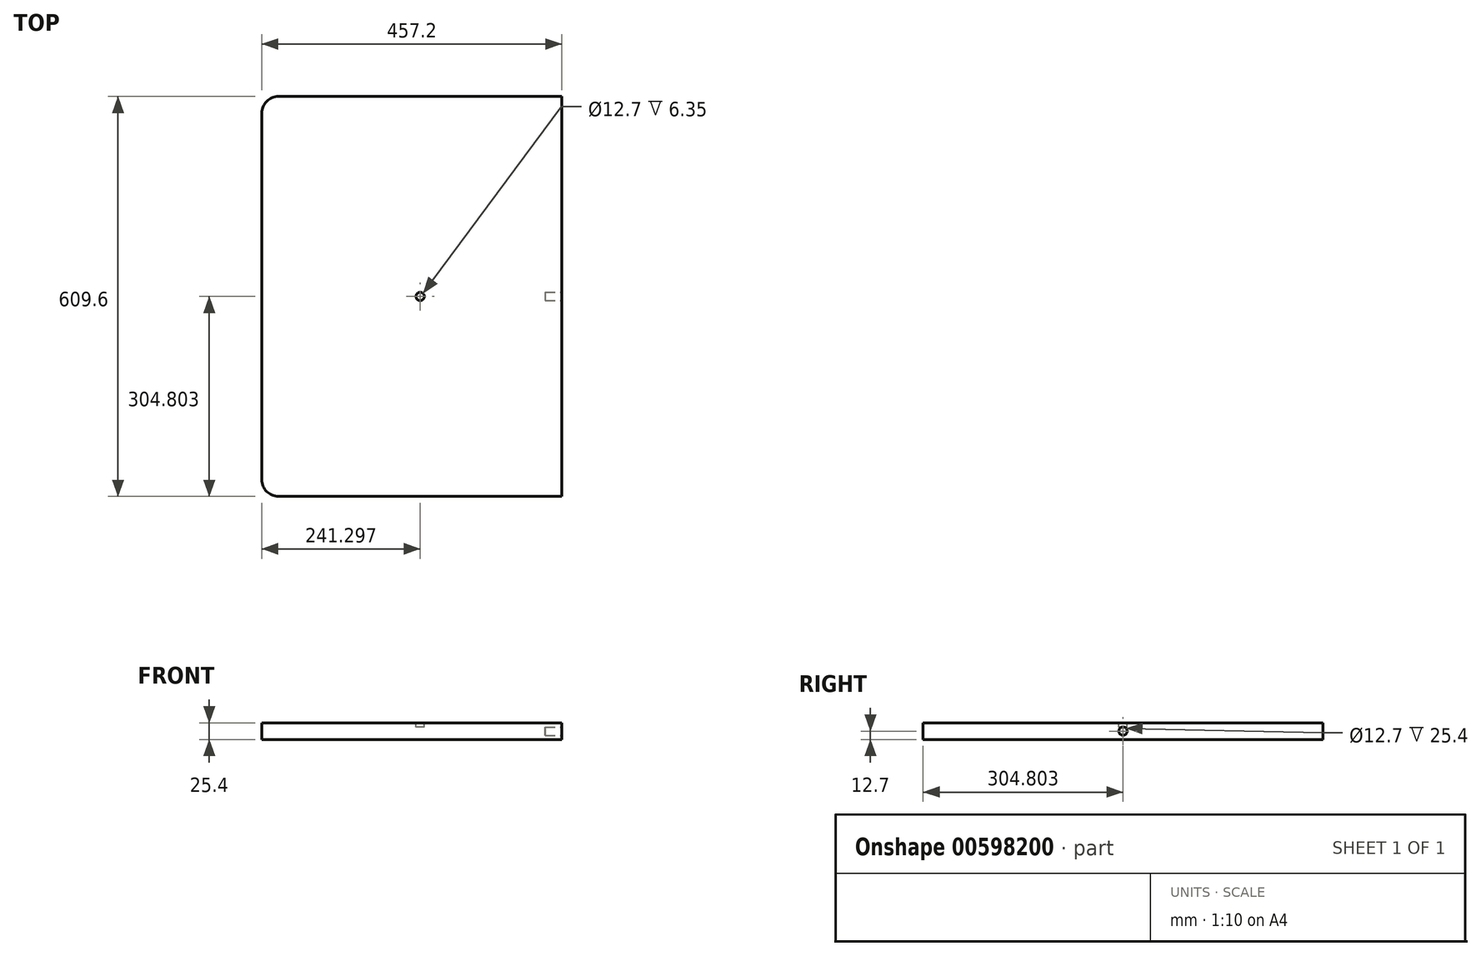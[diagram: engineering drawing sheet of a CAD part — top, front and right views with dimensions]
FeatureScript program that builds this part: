
annotation { "Feature Type Name" : "Feature", "Feature Type Description" : "" }
export const myFeature = defineFeature(function(context is Context, id is Id, definition is map)
    precondition{}
    {
        {
            var Q0;
            Q0=qCreatedBy(makeId("Top.planeOp"),FACE);
            var sketch = newSketch(context, id + "F0", { "sketchPlane" : qUnion([Q0])});
            skLineSegment(sketch, "E0.bottom", {"start": v(255.17, 304.1) * mm, "end": v(-176.63, 304.1) * mm});
            skLineSegment(sketch, "E0.top", {"start": v(255.17, -305.5) * mm, "end": v(-176.63, -305.5) * mm});
            skLineSegment(sketch, "E0.left", {"start": v(255.17, 304.1) * mm, "end": v(255.17, -305.5) * mm});
            skLineSegment(sketch, "E0.right", {"start": v(-202.03, 278.7) * mm, "end": v(-202.03, -280.1) * mm});
            skPoint(sketch, "E0.middle", {"position": v(26.57, -0.7) * mm});
            skPoint(sketch, "E1.visualSharp", {"position": v(-202.03, 304.1) * mm});
            skArc(sketch, "E1.filletArc", {"start": v(-176.63, 304.1) * mm, "mid": v(-194.6, 296.65) * mm, "end": v(-202.03, 278.7) * mm});
            skPoint(sketch, "E2.visualSharp", {"position": v(-202.03, -305.5) * mm});
            skArc(sketch, "E2.filletArc", {"start": v(-202.03, -280.1) * mm, "mid": v(-194.6, -298.07) * mm, "end": v(-176.63, -305.5) * mm});
            skSolve(sketch);
        }
        {
            var Q0;
            Q0=makeQuery(id+"F0.imprint","IMPRINT",FACE,{"disambiguationData":[TD([[makeQuery(id+"F0.imprint","IMPRINT",EDGE,{"derivedFrom":sQuery(id+"F0.wireOp",EDGE,"E0.bottom")}),1.0]])]});
            extrude(context, id + "F1", {"entities" : qUnion([Q0]), "depth" : 25.4 * mm, "offsetDistance" : 25.4 * mm});
        }
        {
            var Q0;
            Q0=makeQuery(id+"F1.opExtrude","SWEPT_FACE",FACE,{"disambiguationData":[OSD([sQuery(id+"F0.wireOp",EDGE,"E0.left")])]});
            var sketch = newSketch(context, id + "F2", { "sketchPlane" : qUnion([Q0])});
            skCircle(sketch, "E3", {"center": v(-0.7, 12.7) * mm, "radius": 6.35 * mm});
            skSolve(sketch);
        }
        {
            var Q0;
            Q0=makeQuery(id+"F2.imprint","IMPRINT",FACE,{"disambiguationData":[TD([[makeQuery(id+"F2.imprint","IMPRINT",EDGE,{"derivedFrom":sQuery(id+"F2.wireOp",EDGE,"E3")}),1.0]])]});
            extrude(context, id + "F3", {"entities" : qUnion([Q0]), "operationType" : NewBodyOperationType.REMOVE, "oppositeDirection" : true, "depth" : 25.4 * mm, "offsetDistance" : 25.4 * mm});
        }
        {
            var Q0;
            Q0=makeQuery(id+"F1.opExtrude","CAP_FACE",FACE,{"disambiguationData":[OSD([sQuery(id+"F0.wireOp",EDGE,"E0.bottom"),sQuery(id+"F0.wireOp",EDGE,"E0.top"),sQuery(id+"F0.wireOp",EDGE,"E0.left"),sQuery(id+"F0.wireOp",EDGE,"E0.right"),sQuery(id+"F0.wireOp",EDGE,"E1.filletArc"),sQuery(id+"F0.wireOp",EDGE,"E2.filletArc")])],"isStart":false});
            var sketch = newSketch(context, id + "F4", { "sketchPlane" : qUnion([Q0])});
            skCircle(sketch, "E4", {"center": v(39.27, -0.7) * mm, "radius": 6.35 * mm});
            skSolve(sketch);
        }
        {
            var Q0;
            Q0=makeQuery(id+"F4.imprint","IMPRINT",FACE,{"disambiguationData":[TD([[makeQuery(id+"F4.imprint","IMPRINT",EDGE,{"derivedFrom":sQuery(id+"F4.wireOp",EDGE,"E4")}),1.0]])]});
            extrude(context, id + "F5", {"entities" : qUnion([Q0]), "operationType" : NewBodyOperationType.REMOVE, "oppositeDirection" : true, "depth" : 6.35 * mm, "offsetDistance" : 25.4 * mm});
        }
    });
